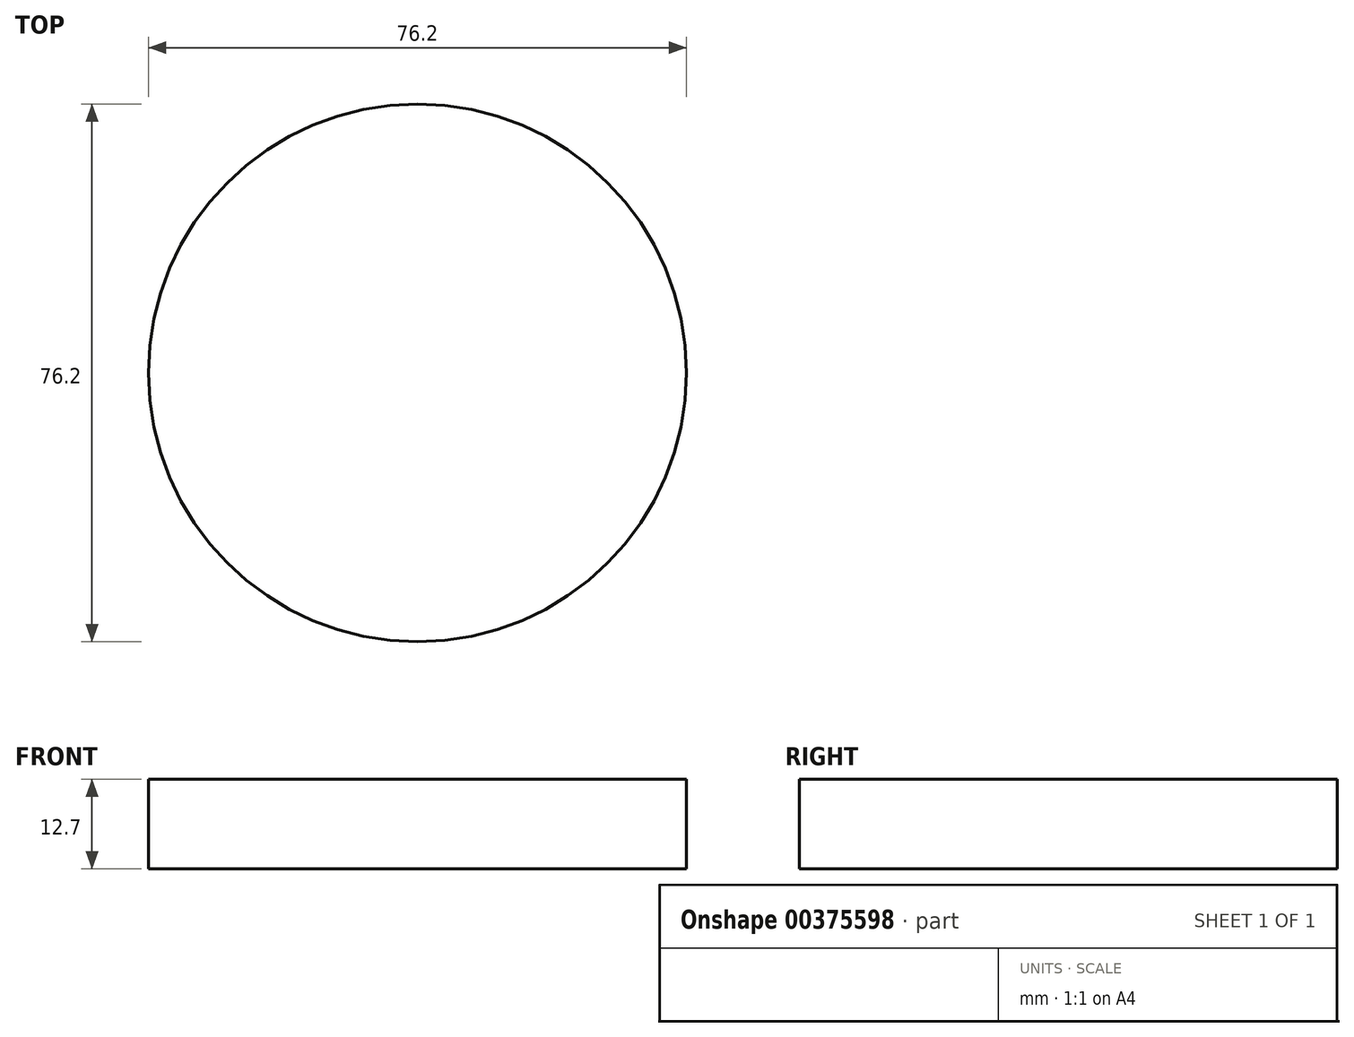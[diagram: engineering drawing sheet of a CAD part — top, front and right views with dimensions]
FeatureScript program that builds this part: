
annotation { "Feature Type Name" : "Feature", "Feature Type Description" : "" }
export const myFeature = defineFeature(function(context is Context, id is Id, definition is map)
    precondition{}
    {
        {
            var Q0;
            Q0=qCreatedBy(makeId("Front.planeOp"),FACE);
            var sketch = newSketch(context, id + "F0", { "sketchPlane" : qUnion([Q0])});
            skLineSegment(sketch, "E0.bottom", {"start": v(0, 0) * mm, "end": v(38.1, 0) * mm});
            skLineSegment(sketch, "E0.top", {"start": v(0, 12.7) * mm, "end": v(38.1, 12.7) * mm});
            skLineSegment(sketch, "E0.left", {"start": v(0, 0) * mm, "end": v(0, 12.7) * mm});
            skLineSegment(sketch, "E0.right", {"start": v(38.1, 0) * mm, "end": v(38.1, 12.7) * mm});
            skLineSegment(sketch, "E1.bottom", {"start": v(0, 12.7) * mm, "end": v(25.4, 12.7) * mm});
            skLineSegment(sketch, "E1.top", {"start": v(0, 76.2) * mm, "end": v(25.4, 76.2) * mm});
            skLineSegment(sketch, "E1.left", {"start": v(0, 12.7) * mm, "end": v(0, 76.2) * mm});
            skLineSegment(sketch, "E1.right", {"start": v(25.4, 12.7) * mm, "end": v(25.4, 76.2) * mm});
            skSolve(sketch);
        }
        {
            var Q0;
            Q0=makeQuery(id+"F0.imprint","IMPRINT",FACE,{"disambiguationData":[TD([[makeQuery(id+"F0.imprint","IMPRINT",EDGE,{"derivedFrom":sQuery(id+"F0.wireOp",EDGE,"E1.bottom")}),1.0]])]});
            var Q1;
            Q1=makeQuery(id+"F0.imprint","IMPRINT",FACE,{"disambiguationData":[TD([[makeQuery(id+"F0.imprint","IMPRINT",EDGE,{"derivedFrom":sQuery(id+"F0.wireOp",EDGE,"E0.bottom")}),1.0]])]});
            var Q2;
            Q2=sQuery(id+"F0.wireOp",EDGE,"E1.left");
            revolve(context, id + "F1", {"entities" : qUnion([Q0, Q1]), "axis" : qUnion([Q2]), "revolveType" : RevolveType.FULL});
        }
    });
